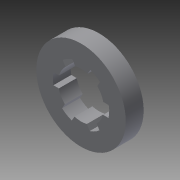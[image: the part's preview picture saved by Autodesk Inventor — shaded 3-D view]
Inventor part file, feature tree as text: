
AUTODESK INVENTOR PART (.ipt)
format: ipt  version: 2014 SP1 (Build 180222100, 222)  size: 103,424 bytes
history: native  units: in
note: dims shown in document units (in); Inventor stores cm internally (conversion verified against a paired STEP export)
features: extrude x1, sketch x1
ambient origin geometry x8: Origin, YZ Plane, XZ Plane, XY Plane, X Axis, Y Axis, Z Axis, Center Point
bodies: Solid1 (feature_tree)
feature tree (2):
  extrude  "Extrusion1"  [1 undecoded]
  sketch  "Sketch1"  dims[d0=0.25in d1=0.0in]
note: 1 required parameter value undecoded (feature->parameter linkage not recoverable at this tier; creation-order binding heuristic only, values carry confidence <= 0.55)
